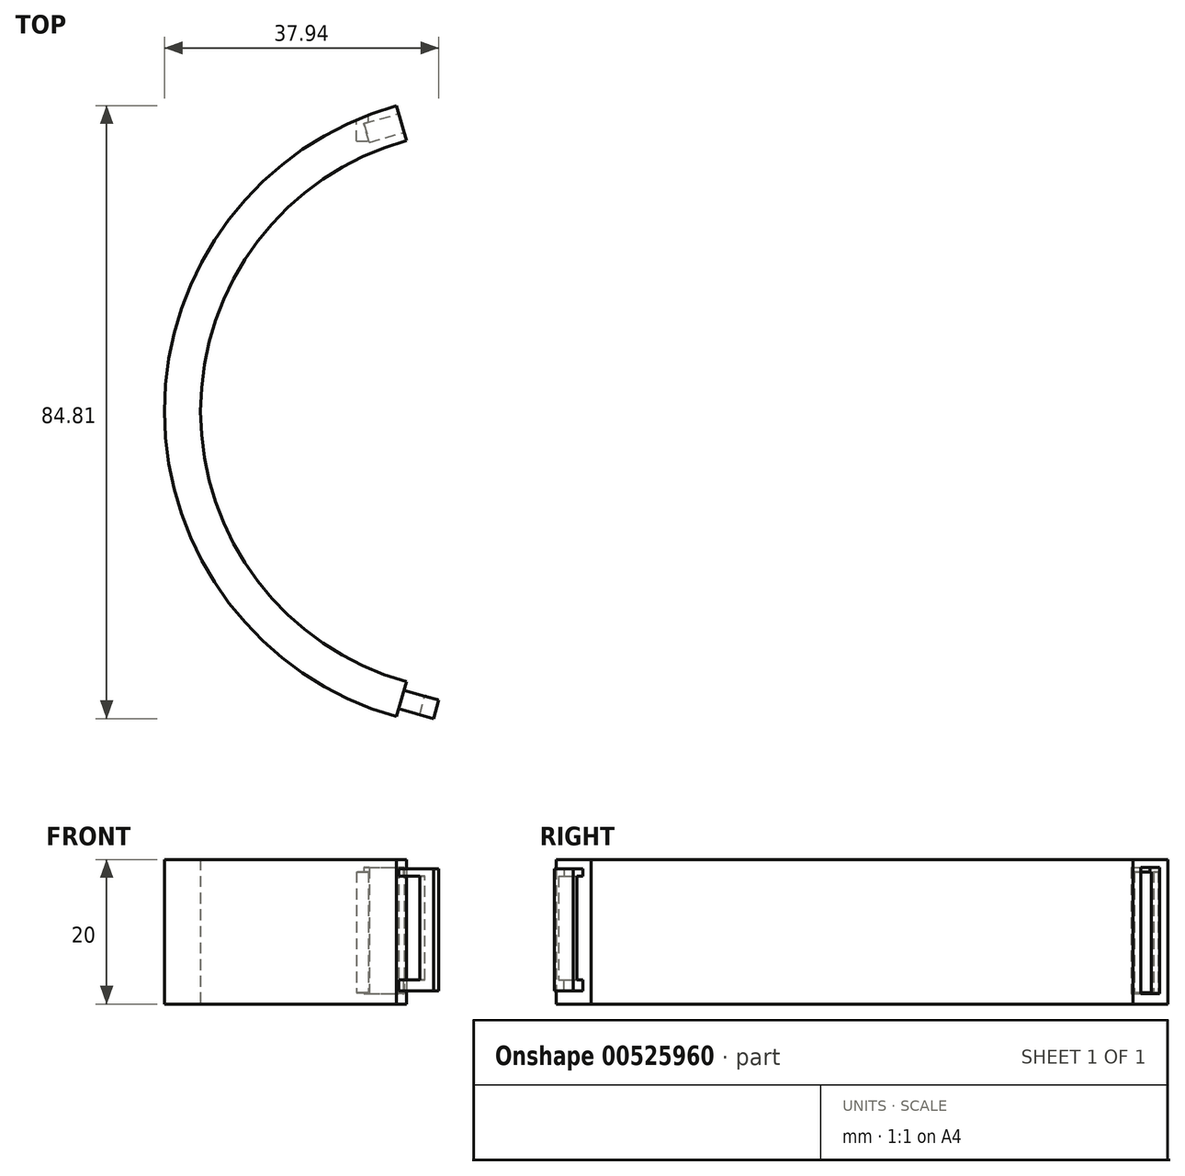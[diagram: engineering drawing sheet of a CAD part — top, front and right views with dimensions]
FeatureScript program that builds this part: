
annotation { "Feature Type Name" : "Feature", "Feature Type Description" : "" }
export const myFeature = defineFeature(function(context is Context, id is Id, definition is map)
    precondition{}
    {
        {
            var Q0;
            Q0=qCreatedBy(makeId("Top.planeOp"),FACE);
            var sketch = newSketch(context, id + "F0", { "sketchPlane" : qUnion([Q0])});
            skArc(sketch, "E0", {"start": v(0, 0) * mm, "mid": v(-28.45, -37.45) * mm, "end": v(0, -74.9) * mm});
            skArc(sketch, "E1.0", {"start": v(-1.34, 4.82) * mm, "mid": v(-33.45, -37.45) * mm, "end": v(-1.34, -79.72) * mm});
            skLineSegment(sketch, "E2", {"start": v(-1.34, 4.82) * mm, "end": v(0, 0) * mm});
            skLineSegment(sketch, "E3", {"start": v(0, -74.9) * mm, "end": v(-1.34, -79.72) * mm});
            skSolve(sketch);
        }
        {
            var Q0;
            Q0 = qSketchRegion(id + "F0", true);
            extrude(context, id + "F1", {"entities" : qUnion([Q0]), "depth" : 20 * mm, "offsetDistance" : 25 * mm});
        }
        {
            var Q0;
            Q0=makeQuery(id+"F1.opExtrude","SWEPT_FACE",FACE,{"disambiguationData":[OSD([sQuery(id+"F0.wireOp",EDGE,"E3")])]});
            var sketch = newSketch(context, id + "F2", { "sketchPlane" : qUnion([Q0])});
            skLineSegment(sketch, "E4", {"start": v(-73.39, 18.74) * mm, "end": v(-76.05, 18.74) * mm});
            skLineSegment(sketch, "E5", {"start": v(-76.05, 18.74) * mm, "end": v(-76.05, 17.7) * mm});
            skLineSegment(sketch, "E6", {"start": v(-76.05, 17.7) * mm, "end": v(-73.39, 17.7) * mm});
            skLineSegment(sketch, "E7", {"start": v(-73.39, 17.7) * mm, "end": v(-73.39, 18.74) * mm});
            skLineSegment(sketch, "E8", {"start": v(-73.39, 1.84) * mm, "end": v(-76.05, 1.84) * mm});
            skPoint(sketch, "E9.end.orphan", {"position": v(-76.05, 0) * mm});
            skLineSegment(sketch, "E10", {"start": v(-73.39, 1.84) * mm, "end": v(-73.39, 3.35) * mm});
            skLineSegment(sketch, "E11", {"start": v(-76.05, 1.84) * mm, "end": v(-76.05, 3.35) * mm});
            skLineSegment(sketch, "E12", {"start": v(-76.05, 3.35) * mm, "end": v(-73.39, 3.35) * mm});
            skSolve(sketch);
        }
        {
            var Q0;
            Q0=makeQuery(id+"F2.imprint","IMPRINT",FACE,{"disambiguationData":[TD([[makeQuery(id+"F2.imprint","IMPRINT",EDGE,{"derivedFrom":sQuery(id+"F2.wireOp",EDGE,"E4")}),1.0]])]});
            var Q1;
            Q1=makeQuery(id+"F2.imprint","IMPRINT",FACE,{"disambiguationData":[TD([[makeQuery(id+"F2.imprint","IMPRINT",EDGE,{"derivedFrom":sQuery(id+"F2.wireOp",EDGE,"E8")}),-1.0]])]});
            extrude(context, id + "F3", {"entities" : qUnion([Q0, Q1]), "operationType" : NewBodyOperationType.ADD, "depth" : 3 * mm, "offsetDistance" : 25 * mm});
        }
        {
            var Q0;
            Q0=makeQuery(id+"F3.opExtrude","CAP_FACE",FACE,{"disambiguationData":[OSD([sQuery(id+"F2.wireOp",EDGE,"E4"),sQuery(id+"F2.wireOp",EDGE,"E5"),sQuery(id+"F2.wireOp",EDGE,"E6"),sQuery(id+"F2.wireOp",EDGE,"E7")])],"isStart":false});
            var sketch = newSketch(context, id + "F4", { "sketchPlane" : qUnion([Q0])});
            skLineSegment(sketch, "E13.bottom", {"start": v(-76.05, 18.74) * mm, "end": v(-73.39, 18.74) * mm});
            skLineSegment(sketch, "E13.top", {"start": v(-76.05, 1.84) * mm, "end": v(-73.39, 1.84) * mm});
            skLineSegment(sketch, "E13.left", {"start": v(-76.05, 18.74) * mm, "end": v(-76.05, 1.84) * mm});
            skLineSegment(sketch, "E13.right", {"start": v(-73.39, 18.74) * mm, "end": v(-73.39, 1.84) * mm});
            skSolve(sketch);
        }
        {
            var Q0;
            {var subQ2=sQuery(id+"F4.wireOp",EDGE,"E13.top");Q0=makeQuery(id+"F4.imprint","IMPRINT",FACE,{"disambiguationData":[TD([[makeQuery(id+"F4.imprint","IMPRINT",EDGE,{"derivedFrom":subQ2}),1.0]])]});}
            var Q1;
            {var subQ0=sQuery(id+"F4.wireOp",EDGE,"E13.bottom");Q1=makeQuery(id+"F4.imprint","IMPRINT",FACE,{"disambiguationData":[TD([[makeQuery(id+"F4.imprint","IMPRINT",EDGE,{"derivedFrom":subQ0}),1.0]])]});}
            extrude(context, id + "F5", {"entities" : qUnion([Q0, Q1]), "operationType" : NewBodyOperationType.ADD, "depth" : 2 * mm, "offsetDistance" : 25 * mm});
        }
        {
            var Q0;
            Q0=makeQuery(id+"F1.opExtrude","SWEPT_FACE",FACE,{"disambiguationData":[OSD([sQuery(id+"F0.wireOp",EDGE,"E2")])]});
            var sketch = newSketch(context, id + "F6", { "sketchPlane" : qUnion([Q0])});
            skLineSegment(sketch, "E14.bottom", {"start": v(1.15, 18.88) * mm, "end": v(3.85, 18.88) * mm});
            skLineSegment(sketch, "E14.top", {"start": v(1.15, 1.42) * mm, "end": v(3.85, 1.42) * mm});
            skLineSegment(sketch, "E14.left", {"start": v(1.15, 18.88) * mm, "end": v(1.15, 1.42) * mm});
            skLineSegment(sketch, "E14.right", {"start": v(3.85, 18.88) * mm, "end": v(3.85, 1.42) * mm});
            skSolve(sketch);
        }
        {
            var Q0;
            Q0=makeQuery(id+"F6.imprint","IMPRINT",FACE,{"disambiguationData":[TD([[makeQuery(id+"F6.imprint","IMPRINT",EDGE,{"derivedFrom":sQuery(id+"F6.wireOp",EDGE,"E14.bottom")}),-1.0]])]});
            extrude(context, id + "F7", {"entities" : qUnion([Q0]), "operationType" : NewBodyOperationType.REMOVE, "oppositeDirection" : true, "depth" : 5 * mm, "offsetDistance" : 25 * mm});
        }
        {
            var Q0;
            Q0=qCreatedBy(makeId("Front.planeOp"),FACE);
            cPlane(context, id + "F8", {"entities" : qUnion([Q0]), "cplaneType" : CPlaneType.OFFSET, "offset" : 4.7 * mm, "oppositeDirection" : true, "width" : 150 * mm, "height" : 150 * mm});
        }
        {
            var Q0;
            Q0=qCreatedBy(id+"F8.planeOp",FACE);
            var sketch = newSketch(context, id + "F9", { "sketchPlane" : qUnion([Q0])});
            skLineSegment(sketch, "E15.bottom", {"start": v(-6.87, 18.28) * mm, "end": v(-5.24, 18.28) * mm});
            skLineSegment(sketch, "E15.top", {"start": v(-6.87, 1.6) * mm, "end": v(-5.24, 1.6) * mm});
            skLineSegment(sketch, "E15.left", {"start": v(-6.87, 18.28) * mm, "end": v(-6.87, 1.6) * mm});
            skLineSegment(sketch, "E15.right", {"start": v(-5.24, 18.28) * mm, "end": v(-5.24, 1.6) * mm});
            skSolve(sketch);
        }
        {
            var Q0;
            Q0=makeQuery(id+"F9.imprint","IMPRINT",FACE,{"disambiguationData":[TD([[makeQuery(id+"F9.imprint","IMPRINT",EDGE,{"derivedFrom":sQuery(id+"F9.wireOp",EDGE,"E15.bottom")}),-1.0]])]});
            extrude(context, id + "F10", {"entities" : qUnion([Q0]), "operationType" : NewBodyOperationType.REMOVE, "depth" : 4.8 * mm, "offsetDistance" : 25 * mm});
        }
    });
